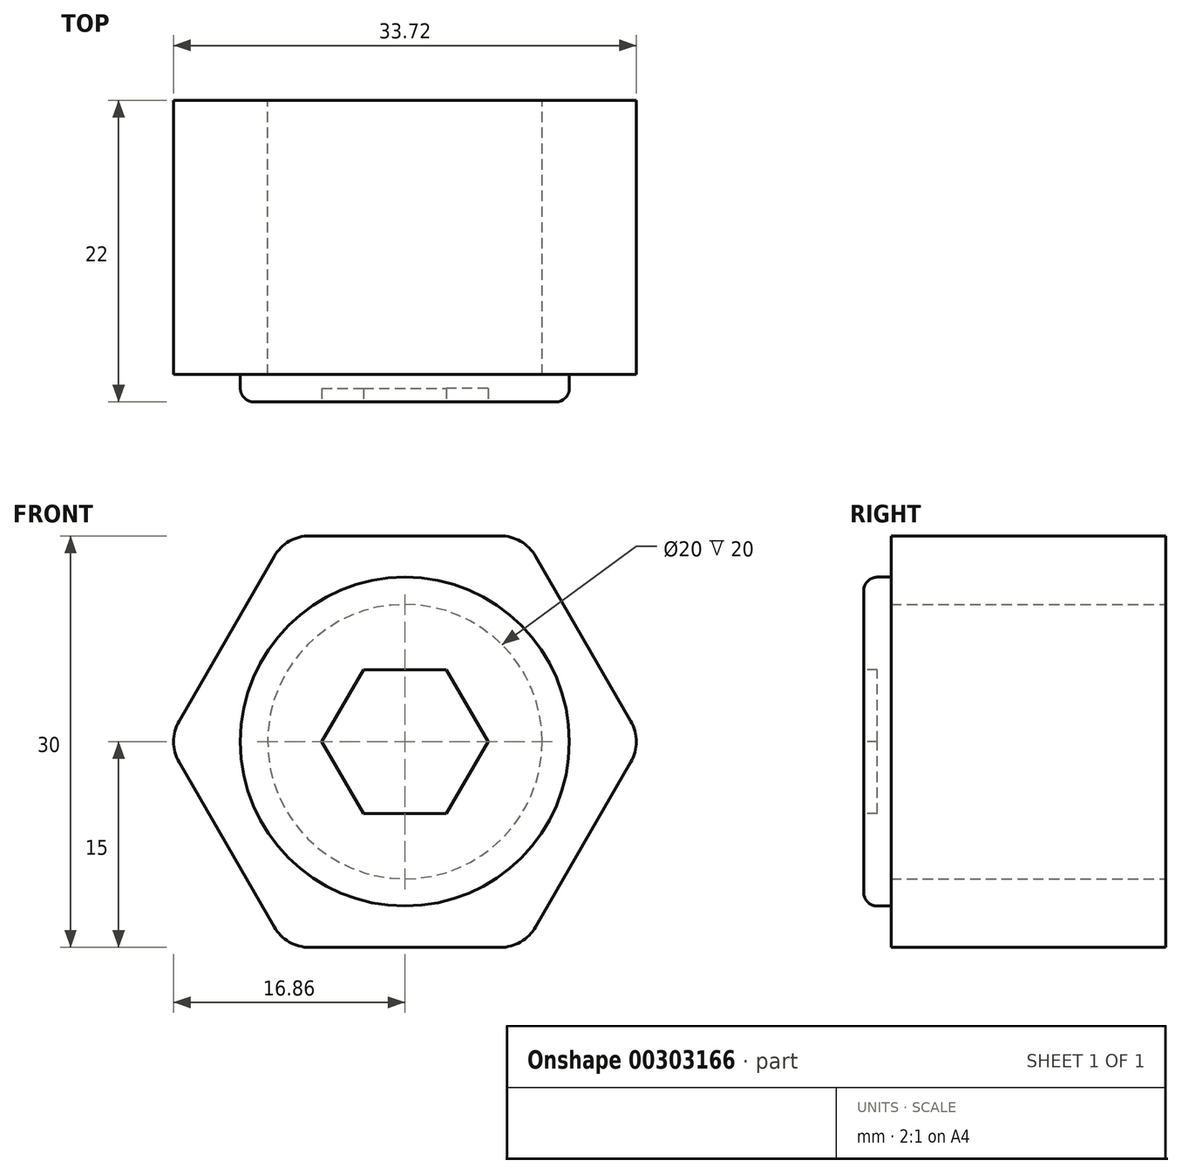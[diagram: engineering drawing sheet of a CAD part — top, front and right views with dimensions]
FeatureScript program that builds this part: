
annotation { "Feature Type Name" : "Feature", "Feature Type Description" : "" }
export const myFeature = defineFeature(function(context is Context, id is Id, definition is map)
    precondition{}
    {
        {
            var Q0;
            Q0=qCreatedBy(makeId("Front.planeOp"),FACE);
            var sketch = newSketch(context, id + "F0", { "sketchPlane" : qUnion([Q0])});
            skCircle(sketch, "E0.cCircle", {"center": v(0, 0) * mm, "radius": 15 * mm, "construction": true});
            skLineSegment(sketch, "E0.0", {"start": v(-6.93, 15) * mm, "end": v(6.93, 15) * mm});
            skLineSegment(sketch, "E0.1", {"start": v(9.53, 13.5) * mm, "end": v(16.45, 1.5) * mm});
            skLineSegment(sketch, "E0.2", {"start": v(16.45, -1.5) * mm, "end": v(9.53, -13.5) * mm});
            skLineSegment(sketch, "E0.3", {"start": v(6.93, -15) * mm, "end": v(-6.93, -15) * mm});
            skLineSegment(sketch, "E0.4", {"start": v(-9.53, -13.5) * mm, "end": v(-16.45, -1.5) * mm});
            skLineSegment(sketch, "E0.5", {"start": v(-16.45, 1.5) * mm, "end": v(-9.53, 13.5) * mm});
            skPoint(sketch, "E0.0.midPoint", {"position": v(0, 15) * mm});
            skCircle(sketch, "E1", {"center": v(0, 0) * mm, "radius": 10 * mm});
            skPoint(sketch, "E2.visualSharp", {"position": v(-8.66, 15) * mm});
            skArc(sketch, "E2.filletArc", {"start": v(-6.93, 15) * mm, "mid": v(-8.43, 14.6) * mm, "end": v(-9.53, 13.5) * mm});
            skPoint(sketch, "E3.visualSharp", {"position": v(-17.32, 0) * mm});
            skArc(sketch, "E3.filletArc", {"start": v(-16.45, 1.5) * mm, "mid": v(-16.86, 0) * mm, "end": v(-16.45, -1.5) * mm});
            skPoint(sketch, "E4.visualSharp", {"position": v(-8.66, -15) * mm});
            skArc(sketch, "E4.filletArc", {"start": v(-9.53, -13.5) * mm, "mid": v(-8.43, -14.6) * mm, "end": v(-6.93, -15) * mm});
            skPoint(sketch, "E5.visualSharp", {"position": v(8.66, -15) * mm});
            skArc(sketch, "E5.filletArc", {"start": v(6.93, -15) * mm, "mid": v(8.43, -14.6) * mm, "end": v(9.53, -13.5) * mm});
            skPoint(sketch, "E6.visualSharp", {"position": v(17.32, 0) * mm});
            skArc(sketch, "E6.filletArc", {"start": v(16.45, -1.5) * mm, "mid": v(16.86, 0) * mm, "end": v(16.45, 1.5) * mm});
            skPoint(sketch, "E7.visualSharp", {"position": v(8.66, 15) * mm});
            skArc(sketch, "E7.filletArc", {"start": v(9.53, 13.5) * mm, "mid": v(8.43, 14.6) * mm, "end": v(6.93, 15) * mm});
            skSolve(sketch);
        }
        {
            var Q0;
            Q0 = qSketchRegion(id + "F0", true);
            extrude(context, id + "F1", {"entities" : qUnion([Q0]), "depth" : 20 * mm});
        }
        {
            var Q0;
            Q0=makeQuery(id+"F1.opExtrude","CAP_FACE",FACE,{"disambiguationData":[OSD([sQuery(id+"F0.wireOp",EDGE,"E0.0"),sQuery(id+"F0.wireOp",EDGE,"E0.1"),sQuery(id+"F0.wireOp",EDGE,"E0.2"),sQuery(id+"F0.wireOp",EDGE,"E0.3"),sQuery(id+"F0.wireOp",EDGE,"E0.4"),sQuery(id+"F0.wireOp",EDGE,"E0.5"),sQuery(id+"F0.wireOp",EDGE,"E1"),sQuery(id+"F0.wireOp",EDGE,"E2.filletArc"),sQuery(id+"F0.wireOp",EDGE,"E3.filletArc"),sQuery(id+"F0.wireOp",EDGE,"E4.filletArc"),sQuery(id+"F0.wireOp",EDGE,"E5.filletArc"),sQuery(id+"F0.wireOp",EDGE,"E6.filletArc"),sQuery(id+"F0.wireOp",EDGE,"E7.filletArc")])],"isStart":false});
            var sketch = newSketch(context, id + "F2", { "sketchPlane" : qUnion([Q0])});
            skCircle(sketch, "E8", {"center": v(0, 0) * mm, "radius": 11.99 * mm});
            skSolve(sketch);
        }
        {
            var Q0;
            Q0 = qSketchRegion(id + "F2", true);
            extrude(context, id + "F3", {"entities" : qUnion([Q0]), "operationType" : NewBodyOperationType.ADD, "depth" : 2 * mm});
        }
        {
            var Q0;
            Q0=makeQuery(id+"F3.opExtrude","CAP_FACE",FACE,{"disambiguationData":[OSD([sQuery(id+"F2.wireOp",EDGE,"E8")])],"isStart":false});
            var Q1;
            Q1=makeQuery(id+"F3.opExtrude","CAP_EDGE",EDGE,{"disambiguationData":[OSD([sQuery(id+"F2.wireOp",EDGE,"E8")])],"isStart":true});
            fillet(context, id + "F4", {"entities" : qUnion([Q0, Q1]), "radius" : 1 * mm, "tangentPropagation" : true, "allowEdgeOverflow" : false});
        }
        {
            var Q0;
            Q0=makeQuery(id+"F3.opExtrude","CAP_FACE",FACE,{"disambiguationData":[OSD([sQuery(id+"F2.wireOp",EDGE,"E8")])],"isStart":false});
            var sketch = newSketch(context, id + "F5", { "sketchPlane" : qUnion([Q0])});
            skCircle(sketch, "E9.cCircle", {"center": v(0, 0) * mm, "radius": 5.24 * mm, "construction": true});
            skLineSegment(sketch, "E9.0", {"start": v(-3.03, 5.24) * mm, "end": v(3.03, 5.24) * mm});
            skLineSegment(sketch, "E9.1", {"start": v(3.03, 5.24) * mm, "end": v(6.06, 0) * mm});
            skLineSegment(sketch, "E9.2", {"start": v(6.06, 0) * mm, "end": v(3.03, -5.24) * mm});
            skLineSegment(sketch, "E9.3", {"start": v(3.03, -5.24) * mm, "end": v(-3.03, -5.24) * mm});
            skLineSegment(sketch, "E9.4", {"start": v(-3.03, -5.24) * mm, "end": v(-6.06, 0) * mm});
            skLineSegment(sketch, "E9.5", {"start": v(-6.06, 0) * mm, "end": v(-3.03, 5.24) * mm});
            skPoint(sketch, "E9.0.midPoint", {"position": v(0, 5.24) * mm});
            skSolve(sketch);
        }
        {
            var Q0;
            Q0 = qSketchRegion(id + "F5", true);
            extrude(context, id + "F6", {"entities" : qUnion([Q0]), "operationType" : NewBodyOperationType.REMOVE, "oppositeDirection" : true, "depth" : 1 * mm});
        }
    });
